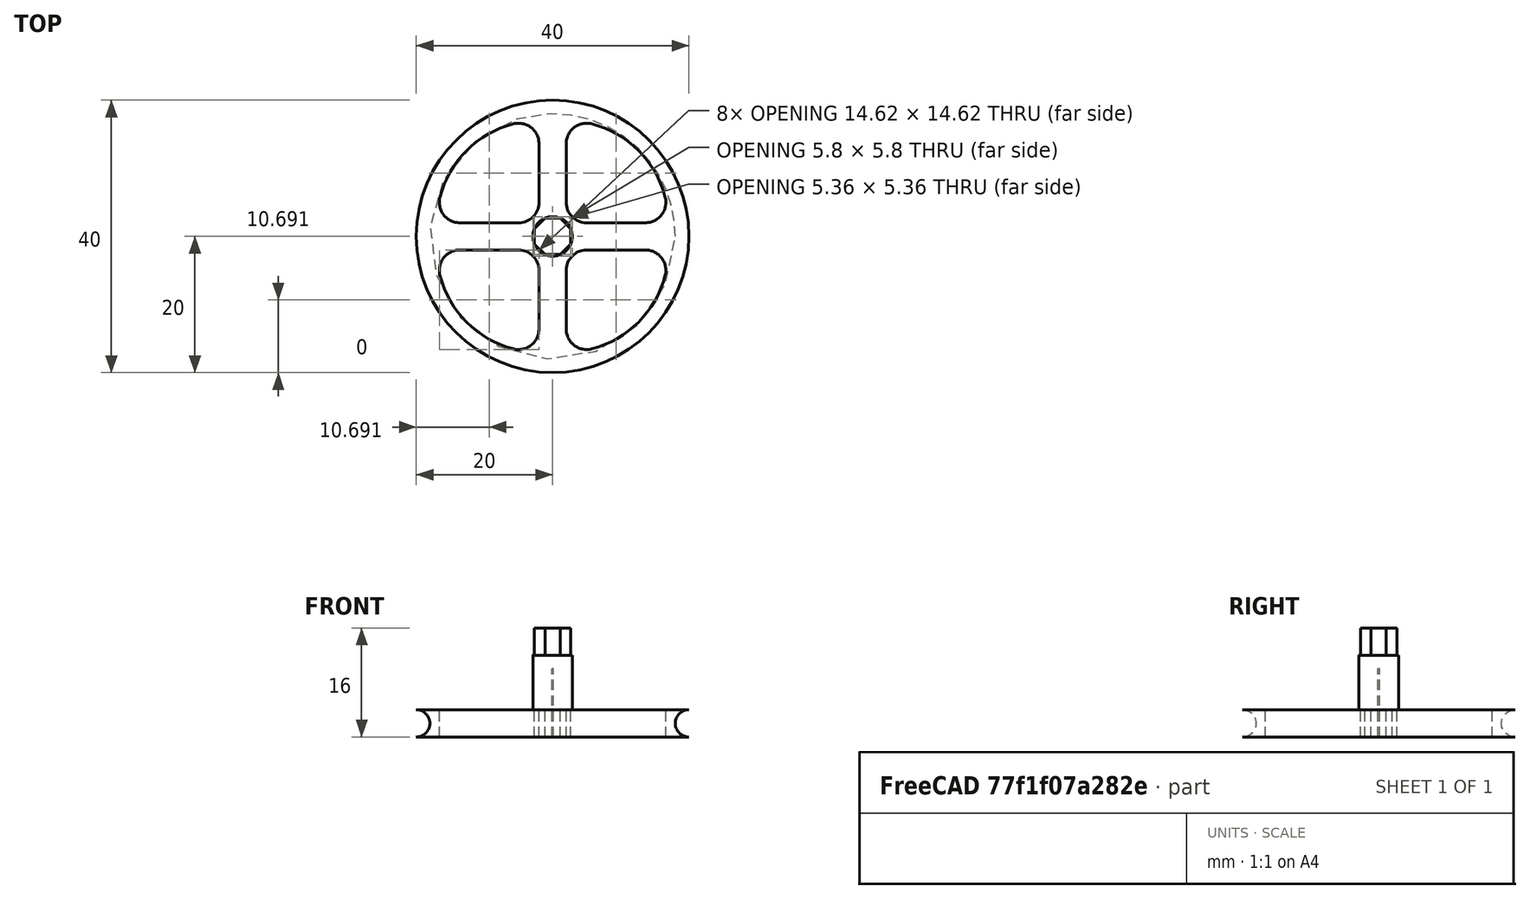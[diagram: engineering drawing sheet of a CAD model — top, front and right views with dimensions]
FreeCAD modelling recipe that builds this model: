
FCSTD DOCUMENT  (FreeCAD 0.18.1R)
Label: wheel left front techdraw
License: All rights reserved
LicenseURL: http://en.wikipedia.org/wiki/All_rights_reserved
objects: TechDraw::DrawViewDimension×8, PartDesign::Plane×4, TechDraw::DrawProjGroupItem×4, Part::Cylinder×3, Sketcher::SketchObject×3, PartDesign::Fillet×3, PartDesign::Body×3, PartDesign::FeatureBase×2, PartDesign::Pocket×2, App::Part×2, Part::MultiFuse×2, Part::Torus×1, Part::Cut×1, App::MeasureDistance×1, PartDesign::ShapeBinder×1, PartDesign::Pad×1, TechDraw::DrawSVGTemplate×1, TechDraw::DrawProjGroup×1, TechDraw::DrawPage×1
note: 29 computed .brp shape members not serialized (recipe doc carries the construction recipe); baked Part::Feature solids carry a one-line shape summary decoded from their .brp

FEATURE [Part::Cylinder] Cylinder
  Angle = 360
  AttacherType = Attacher::AttachEngine3D
  Height = 4
  Radius = 20
FEATURE [Part::Cylinder] Cylinder001
  Angle = 360
  AttacherType = Attacher::AttachEngine3D
  Height = 10
  Radius = 0.1
FEATURE [PartDesign::FeatureBase] BaseFeature
  BaseFeature = -> Cylinder
FEATURE [PartDesign::Plane] DatumPlane
  Length = 47.9863
  MapMode = 5
  Placement = pos=(0,0,0) rot=(1,0,0;3.14159rad)
  ResizeMode = 0
  Support = -> [BaseFeature]
  Width = 47.8497
FEATURE [Sketcher::SketchObject] Sketch001
  MapMode = 5
  Placement = pos=(0,0,0) rot=(1,0,0;3.14159rad)
  Support = -> [DatumPlane]
  sketch-geometry (12):
    g0: LineSegment StartX=2 StartY=17 StartZ=0 EndX=2 EndY=2 EndZ=0
    g1: LineSegment StartX=-2 StartY=17 StartZ=0 EndX=-2 EndY=2 EndZ=0
    g2: LineSegment StartX=2 StartY=2 StartZ=0 EndX=17 EndY=2 EndZ=0
    g3: LineSegment StartX=2 StartY=-2 StartZ=0 EndX=17 EndY=-2 EndZ=0
    g4: LineSegment StartX=-2 StartY=-2 StartZ=0 EndX=-2 EndY=-17 EndZ=0
    g5: LineSegment StartX=-17 StartY=-2 StartZ=0 EndX=-2 EndY=-2 EndZ=0
    g6: LineSegment StartX=-17 StartY=2 StartZ=0 EndX=-2 EndY=2 EndZ=0
    g7: LineSegment StartX=2 StartY=-2 StartZ=0 EndX=2 EndY=-17 EndZ=0
    g8: ArcOfCircle CenterX=2 CenterY=2 CenterZ=0 NormalX=0 NormalY=0 NormalZ=1 AngleXU=0 Radius=15 StartAngle=0 EndAngle=1.5708
    g9: ArcOfCircle CenterX=-2 CenterY=2 CenterZ=0 NormalX=0 NormalY=0 NormalZ=1 AngleXU=0 Radius=15 StartAngle=1.5708 EndAngle=3.14159
    g10: ArcOfCircle CenterX=-2 CenterY=-2 CenterZ=0 NormalX=0 NormalY=0 NormalZ=1 AngleXU=0 Radius=15 StartAngle=3.14159 EndAngle=4.71239
    g11: ArcOfCircle CenterX=2 CenterY=-2 CenterZ=0 NormalX=0 NormalY=0 NormalZ=1 AngleXU=0 Radius=15 StartAngle=4.71239 EndAngle=6.28319
  constraints (35):
    c: Vertical(g0)
    c: Vertical(g1)
    c: Horizontal(g2)
    c: Horizontal(g3)
    c: Vertical(g4)
    c: Horizontal(g6)
    c: DistanceX(g0) = 2
    c: DistanceY(g0) = 17
    c: DistanceY(g0) = 2
    c: Coincident(g0,g2)
    c: DistanceX(g3) = 2
    c: Coincident(g3,g7)
    c: DistanceX(g3) = 17
    c: DistanceY(g7) = -17
    c: DistanceX(g5) = -2
    c: DistanceY(g5) = -2
    c: Coincident(g5,g4)
    c: DistanceY(g4) = -17
    c: DistanceX(g5) = -17
    c: DistanceX(g6) = -2
    c: DistanceX(g6) = -17
    c: DistanceY(g6) = 2
    c: Coincident(g6,g1)
    c: Coincident(g8,g0)
    c: Coincident(g8,g0)
    c: Coincident(g9,g1)
    c: Coincident(g9,g1)
    c: Coincident(g9,g6)
    c: Coincident(g10,g4)
    c: Coincident(g10,g4)
    c: Coincident(g10,g5)
    c: Coincident(g11,g3)
    c: Coincident(g11,g3)
    c: Coincident(g11,g7)
    c: Coincident(g8,g2)
FEATURE [PartDesign::Pocket] Pocket
  BaseFeature = -> BaseFeature
  Length = 5
  Length2 = 100
  Profile = -> Sketch001
  Type = 1
FEATURE [PartDesign::Fillet] Fillet
  Base = -> Pocket [Edge39]
  BaseFeature = -> Pocket
  Radius = 3
FEATURE [PartDesign::Fillet] Fillet001
  Base = -> Fillet [Edge27,Edge39,Edge41,Edge17,Edge26,Edge32,Edge35]
  BaseFeature = -> Fillet
  Radius = 3
FEATURE [PartDesign::Fillet] Fillet002
  Base = -> Fillet001 [Edge56,Edge46,Edge42,Edge30]
  BaseFeature = -> Fillet001
  Radius = 3
FEATURE [PartDesign::Body] Body
  BaseFeature = -> Cylinder
  Group = -> [BaseFeature,DatumPlane,Sketch001,Pocket,Fillet,Fillet001,Fillet002]
  Origin = -> Origin
  Tip = -> Fillet002
FEATURE [Part::Torus] Torus
  Angle1 = -180
  Angle2 = 180
  Angle3 = 360
  AttacherType = Attacher::AttachEngine3D
  Placement = pos=(0,0,2) rot=(0,0,1;0rad)
  Radius1 = 20
  Radius2 = 2
FEATURE [Part::Cut] Cut
  Base = -> Body
  Tool = -> Torus
FEATURE [PartDesign::FeatureBase] BaseFeature001
  BaseFeature = -> Cut
FEATURE [PartDesign::Plane] DatumPlane001
  Length = 24
  MapMode = 5
  Placement = pos=(0,0,0) rot=(1,0,0;3.14159rad)
  ResizeMode = 0
  Support = -> [BaseFeature001]
  Width = 24
FEATURE [PartDesign::Plane] DatumPlane002
  Length = 24
  MapMode = 5
  Placement = pos=(0,0,0) rot=(1,0,0;3.14159rad)
  ResizeMode = 0
  Support = -> [BaseFeature001]
  Width = 24
FEATURE [Sketcher::SketchObject] Sketch
  MapMode = 5
  Placement = pos=(0,0,0) rot=(1,0,0;3.14159rad)
  Support = -> [DatumPlane002]
  sketch-geometry (9):
    g0: LineSegment StartX=1.10978 StartY=-2.67925 StartZ=0 EndX=2.67925 EndY=-1.10978 EndZ=0
    g1: LineSegment StartX=2.67925 StartY=-1.10978 StartZ=0 EndX=2.67925 EndY=1.10978 EndZ=0
    g2: LineSegment StartX=2.67925 StartY=1.10978 StartZ=0 EndX=1.10978 EndY=2.67925 EndZ=0
    g3: LineSegment StartX=1.10978 StartY=2.67925 StartZ=0 EndX=-1.10978 EndY=2.67925 EndZ=0
    g4: LineSegment StartX=-1.10978 StartY=2.67925 StartZ=0 EndX=-2.67925 EndY=1.10978 EndZ=0
    g5: LineSegment StartX=-2.67925 StartY=1.10978 StartZ=0 EndX=-2.67925 EndY=-1.10978 EndZ=0
    g6: LineSegment StartX=-2.67925 StartY=-1.10978 StartZ=0 EndX=-1.10978 EndY=-2.67925 EndZ=0
    g7: LineSegment StartX=-1.10978 StartY=-2.67925 StartZ=0 EndX=1.10978 EndY=-2.67925 EndZ=0
    g8: Circle [constr] CenterX=0 CenterY=0 CenterZ=0 NormalX=0 NormalY=0 NormalZ=1 AngleXU=0 Radius=2.9
  constraints (20):
    c: Coincident(g0,g1)
    c: Coincident(g1,g2)
    c: Coincident(g2,g3)
    c: Coincident(g3,g4)
    c: Coincident(g4,g5)
    c: Coincident(g5,g6)
    c: Coincident(g6,g7)
    c: Coincident(g7,g0)
    c: Equal(g0, g1-g7) x7
    c: PointOnObject(g0,g8)
    c: PointOnObject(g1,g8)
    c: PointOnObject(g2,g8)
    c: PointOnObject(g3,g8)
    c: PointOnObject(g4,g8)
    c: PointOnObject(g5,g8)
    c: PointOnObject(g6,g8)
    c: PointOnObject(g7,g8)
    c: Coincident(g8,g-1)
    c: Radius(g8) = 2.9
    c: DistanceX(g1,g0) = 0
FEATURE [PartDesign::Pocket] Pocket001
  BaseFeature = -> BaseFeature001
  Length = 5
  Length2 = 100
  Profile = -> Sketch
  Type = 0
FEATURE [PartDesign::Body] Body001
  BaseFeature = -> Cut
  Group = -> [BaseFeature001,DatumPlane001,DatumPlane002,Sketch,Pocket001]
  Origin = -> Origin001
  Tip = -> Pocket001
FEATURE [Part::Cylinder] Cylinder002
  Angle = 360
  AttacherType = Attacher::AttachEngine3D
  Height = 12
  Radius = 2.9
FEATURE [App::MeasureDistance] Distance  label="Distance: 4.03 mm"
  Distance = 4.03426
  P1 = (-19.6792,-3.42447,0)
  P2 = (-19.7612,-2.90625,4)
FEATURE [App::Part] Part
  Origin = -> Origin002
FEATURE [PartDesign::ShapeBinder] CopyFusion
  TraceSupport = false
FEATURE [PartDesign::Plane] DatumPlane003
  Length = 24
  MapMode = 5
  Placement = pos=(0,0,12) rot=(0,0,1;0rad)
  ResizeMode = 0
  Support = -> [CopyFusion]
  Width = 24
FEATURE [Sketcher::SketchObject] Sketch002
  MapMode = 5
  Placement = pos=(0,0,12) rot=(0,0,1;0rad)
  Support = -> [DatumPlane003]
  sketch-geometry (9):
    g0: LineSegment StartX=1.10978 StartY=2.67925 StartZ=0 EndX=-1.10978 EndY=2.67925 EndZ=0
    g1: LineSegment StartX=-1.10978 StartY=2.67925 StartZ=0 EndX=-2.67925 EndY=1.10978 EndZ=0
    g2: LineSegment StartX=-2.67925 StartY=1.10978 StartZ=0 EndX=-2.67925 EndY=-1.10978 EndZ=0
    g3: LineSegment StartX=-2.67925 StartY=-1.10978 StartZ=0 EndX=-1.10978 EndY=-2.67925 EndZ=0
    g4: LineSegment StartX=-1.10978 StartY=-2.67925 StartZ=0 EndX=1.10978 EndY=-2.67925 EndZ=0
    g5: LineSegment StartX=1.10978 StartY=-2.67925 StartZ=0 EndX=2.67925 EndY=-1.10978 EndZ=0
    g6: LineSegment StartX=2.67925 StartY=-1.10978 StartZ=0 EndX=2.67925 EndY=1.10978 EndZ=0
    g7: LineSegment StartX=2.67925 StartY=1.10978 StartZ=0 EndX=1.10978 EndY=2.67925 EndZ=0
    g8: Circle [constr] CenterX=0 CenterY=0 CenterZ=0 NormalX=0 NormalY=0 NormalZ=1 AngleXU=0 Radius=2.9
  constraints (20):
    c: Coincident(g0,g1)
    c: Coincident(g1,g2)
    c: Coincident(g2,g3)
    c: Coincident(g3,g4)
    c: Coincident(g4,g5)
    c: Coincident(g5,g6)
    c: Coincident(g6,g7)
    c: Coincident(g7,g0)
    c: Equal(g0, g1-g7) x7
    c: PointOnObject(g0,g8)
    c: PointOnObject(g1,g8)
    c: PointOnObject(g2,g8)
    c: PointOnObject(g3,g8)
    c: PointOnObject(g4,g8)
    c: PointOnObject(g5,g8)
    c: PointOnObject(g6,g8)
    c: PointOnObject(g7,g8)
    c: Radius(g8) = 2.9
    c: Coincident(g-1,g8)
    c: DistanceX(g6,g5) = 0
FEATURE [PartDesign::Pad] Pad
  Length = 4
  Length2 = 100
  Placement = pos=(0,0,12) rot=(0,0,1;0rad)
  Profile = -> Sketch002
  Type = 0
FEATURE [PartDesign::Body] Body002
  Group = -> [DatumPlane003,CopyFusion,Sketch002,Pad]
  Origin = -> Origin003
  Tip = -> Pad
FEATURE [App::Part] Part001
  Group = -> [Body002]
  Origin = -> Origin004
FEATURE [Part::MultiFuse] Fusion
  Shapes = -> [Pocket001,Cylinder002]
FEATURE [Part::MultiFuse] Fusion001
  Shapes = -> [Pad,Fusion]
FEATURE [TechDraw::DrawSVGTemplate] Template
  EditableTexts = Designed_by_Name=Designed by Name; Drawing_number=Drawing number; FC-Date=Date; FC-SC=Scale; FC-SH=Sheet; FC-Title=Title; Subtitle=Subtitle; Weight=Weight
  Height = 210
  Orientation = 1
  Width = 297
FEATURE [TechDraw::DrawProjGroupItem] ProjItem  label="Front"
  CoarseView = false
  Direction = (0,-1,0)
  Focus = 100
  HardHidden = false
  IsoCount = 0
  IsoHidden = false
  IsoVisible = false
  LockPosition = true
  Perspective = false
  Rotation = 0
  RotationVector = (1,0,0)
  ScaleType = 2
  SeamHidden = false
  SeamVisible = false
  SmoothHidden = false
  SmoothVisible = false
  Source = -> [Fusion001]
  Type = 0
  X = 0
  Y = 0
FEATURE [TechDraw::DrawProjGroupItem] ProjItem001  label="Left"
  CoarseView = false
  Direction = (-1,-1e-16,0)
  Focus = 100
  HardHidden = false
  IsoCount = 0
  IsoHidden = false
  IsoVisible = false
  LockPosition = false
  Perspective = false
  Rotation = 0
  RotationVector = (1e-16,-1,0)
  ScaleType = 2
  SeamHidden = false
  SeamVisible = false
  SmoothHidden = false
  SmoothVisible = false
  Source = -> [Fusion001]
  Type = 1
  X = 55
  Y = 0
FEATURE [TechDraw::DrawProjGroupItem] ProjItem002  label="FrontTopLeft"
  CoarseView = false
  Direction = (-1,-1,1)
  Focus = 100
  HardHidden = false
  IsoCount = 0
  IsoHidden = false
  IsoVisible = false
  LockPosition = false
  Perspective = false
  Rotation = 0
  RotationVector = (1,-1,0)
  ScaleType = 2
  SeamHidden = false
  SeamVisible = false
  SmoothHidden = false
  SmoothVisible = false
  Source = -> [Fusion001]
  Type = 6
  X = 55
  Y = -55
FEATURE [TechDraw::DrawProjGroupItem] ProjItem003  label="Top"
  CoarseView = false
  Direction = (0,0,1)
  Focus = 100
  HardHidden = false
  IsoCount = 0
  IsoHidden = false
  IsoVisible = false
  LockPosition = false
  Perspective = false
  Rotation = 0
  RotationVector = (1,0,0)
  ScaleType = 2
  SeamHidden = false
  SeamVisible = false
  SmoothHidden = false
  SmoothVisible = false
  Source = -> [Fusion001]
  Type = 4
  X = 0
  Y = -55
FEATURE [TechDraw::DrawProjGroup] ProjGroup
  Anchor = -> ProjItem
  AutoDistribute = true
  LockPosition = false
  ProjectionType = 1
  Rotation = 0
  ScaleType = 0
  Source = -> [Fusion001]
  Views = -> [ProjItem,ProjItem001,ProjItem002,ProjItem003]
  X = 97.1013
  Y = 154.062
  spacingX = 15
  spacingY = 15
FEATURE [TechDraw::DrawViewDimension] Dimension
  Arbitrary = false
  FormatSpec = %.2f
  LockPosition = false
  MeasureType = 1
  OverTolerance = 0
  References2D = -> [ProjItem]
  Rotation = 0
  ScaleType = 0
  Type = 1
  UnderTolerance = 0
  X = 3.38007
  Y = 23.2283
FEATURE [TechDraw::DrawViewDimension] Dimension001
  Arbitrary = false
  FormatSpec = %.2f
  LockPosition = false
  MeasureType = 1
  OverTolerance = 0
  References2D = -> [ProjItem]
  Rotation = 0
  ScaleType = 0
  Type = 2
  UnderTolerance = 0
  X = 13.4158
  Y = 0
FEATURE [TechDraw::DrawViewDimension] Dimension002
  Arbitrary = false
  FormatSpec = %.2f
  LockPosition = false
  MeasureType = 1
  OverTolerance = 0
  References2D = -> [ProjItem]
  Rotation = 0
  ScaleType = 0
  Type = 2
  UnderTolerance = 0
  X = -14.4089
  Y = 6.56334
FEATURE [TechDraw::DrawViewDimension] Dimension003
  Arbitrary = false
  FormatSpec = %.2f
  LockPosition = false
  MeasureType = 1
  OverTolerance = 0
  References2D = -> [ProjItem003]
  Rotation = 0
  ScaleType = 0
  Type = 1
  UnderTolerance = 0
  X = -11.9176
  Y = 27.168
FEATURE [TechDraw::DrawViewDimension] Dimension004
  Arbitrary = false
  FormatSpec = R%.2f
  LockPosition = false
  MeasureType = 1
  OverTolerance = 0
  References2D = -> [ProjItem003]
  Rotation = 0
  ScaleType = 0
  Type = 4
  UnderTolerance = 0
  X = 16.3005
  Y = 26.7328
FEATURE [TechDraw::DrawViewDimension] Dimension005
  Arbitrary = false
  FormatSpec = ⌀%.2f
  LockPosition = false
  MeasureType = 1
  OverTolerance = 0
  References2D = -> [ProjItem003]
  Rotation = 0
  ScaleType = 0
  Type = 5
  UnderTolerance = 0
  X = 2.389
  Y = -30.1129
FEATURE [TechDraw::DrawViewDimension] Dimension006
  Arbitrary = false
  FormatSpec = R%.2f
  LockPosition = false
  MeasureType = 1
  OverTolerance = 0
  References2D = -> [ProjItem003]
  Rotation = 0
  ScaleType = 0
  Type = 4
  UnderTolerance = 0
  X = 24.3855
  Y = 22.4295
FEATURE [TechDraw::DrawViewDimension] Dimension007
  Arbitrary = false
  FormatSpec = %.2f
  LockPosition = false
  MeasureType = 1
  OverTolerance = 0
  References2D = -> [ProjItem003]
  Rotation = 0
  ScaleType = 0
  Type = 1
  UnderTolerance = 0
  X = -1.66023
  Y = 12.5652
FEATURE [TechDraw::DrawPage] Page
  KeepUpdated = true
  ProjectionType = 0
  Template = -> Template
  Views = -> [ProjGroup,Dimension,Dimension001,Dimension002,Dimension003,Dimension004,Dimension005,Dimension006,Dimension007]
